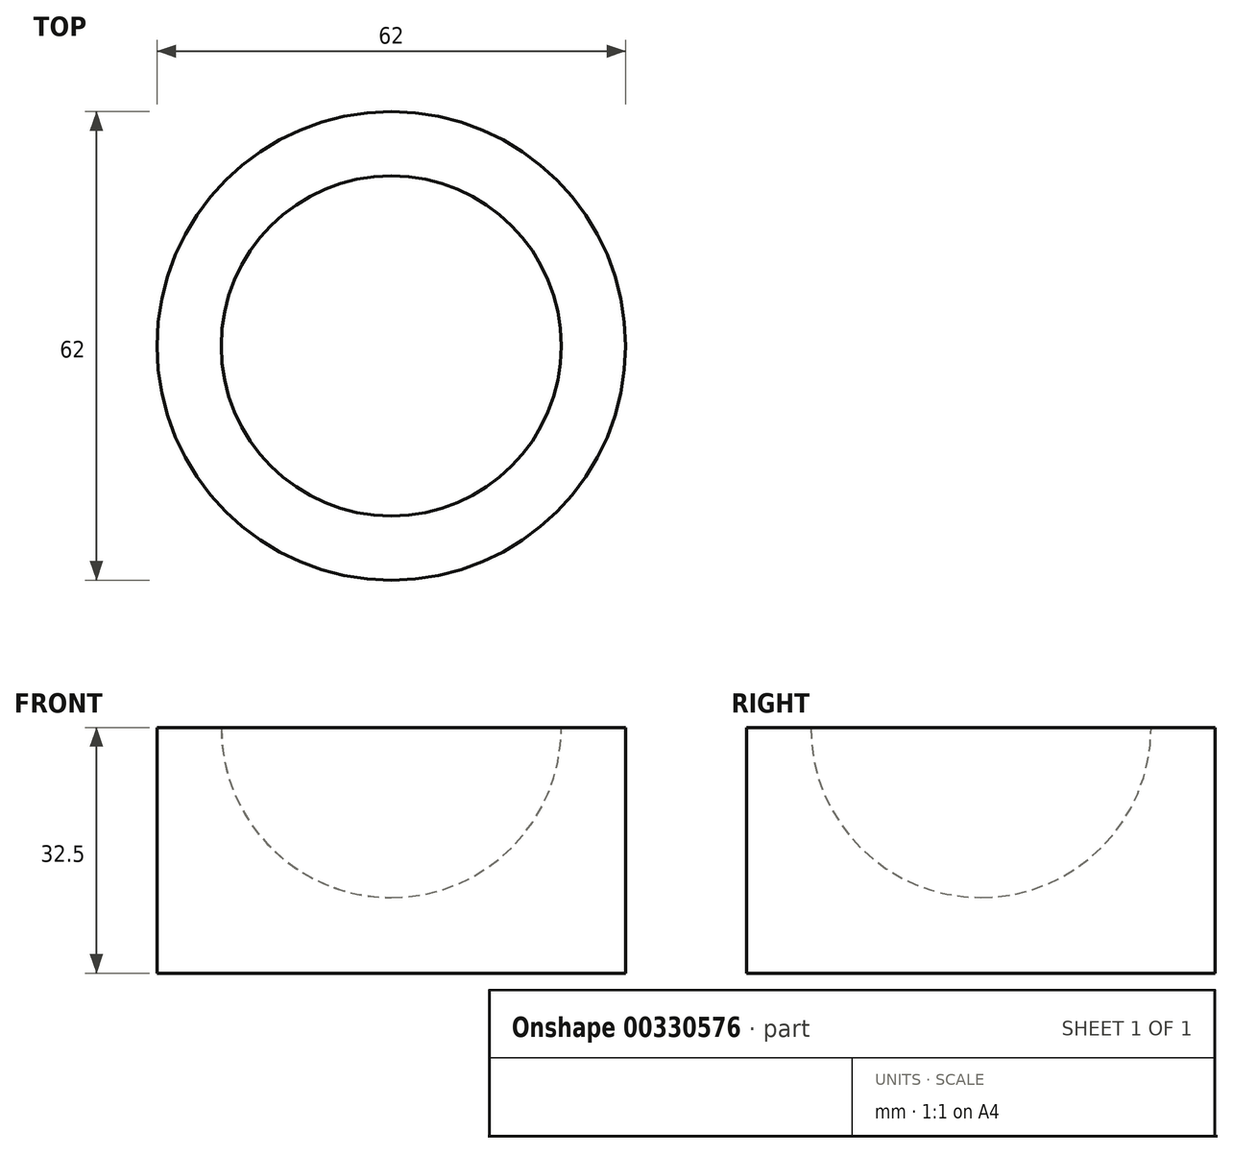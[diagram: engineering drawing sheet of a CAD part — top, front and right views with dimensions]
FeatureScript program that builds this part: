
annotation { "Feature Type Name" : "Feature", "Feature Type Description" : "" }
export const myFeature = defineFeature(function(context is Context, id is Id, definition is map)
    precondition{}
    {
        {
            var Q0;
            Q0=qCreatedBy(makeId("Front.planeOp"),FACE);
            var sketch = newSketch(context, id + "F0", { "sketchPlane" : qUnion([Q0])});
            skLineSegment(sketch, "E0.bottom", {"start": v(0, 0) * mm, "end": v(31, 0) * mm});
            skLineSegment(sketch, "E0.top", {"start": v(0, 32.5) * mm, "end": v(8.5, 32.5) * mm});
            skLineSegment(sketch, "E0.left", {"start": v(0, 0) * mm, "end": v(0, 32.5) * mm});
            skLineSegment(sketch, "E0.right", {"start": v(31, 0) * mm, "end": v(31, 10) * mm});
            skArc(sketch, "E1", {"start": v(8.5, 32.5) * mm, "mid": v(15.1, 16.6) * mm, "end": v(31, 10) * mm});
            skSolve(sketch);
        }
        {
            var Q0;
            Q0=qSketchRegion(id+"F0",true);
            var Q1;
            Q1=sQuery(id+"F0.wireOp",EDGE,"E0.right");
            revolve(context, id + "F1", {"entities" : qUnion([Q0]), "axis" : qUnion([Q1]), "revolveType" : RevolveType.FULL});
        }
    });
